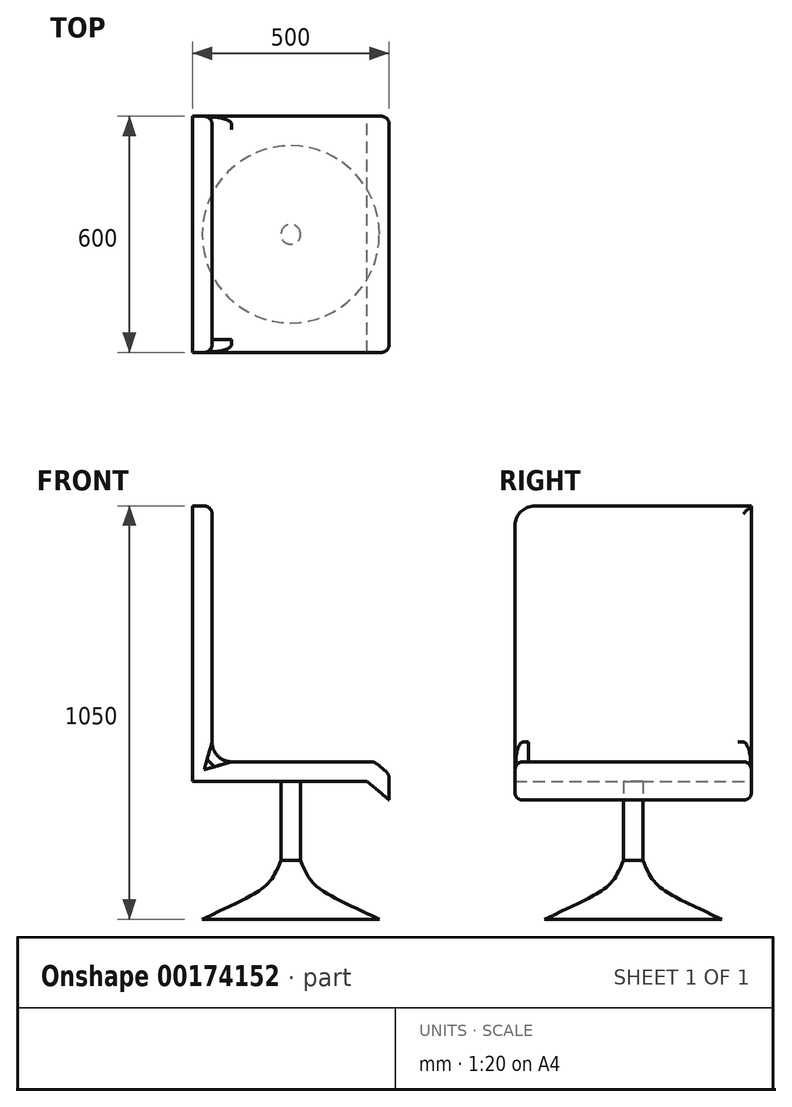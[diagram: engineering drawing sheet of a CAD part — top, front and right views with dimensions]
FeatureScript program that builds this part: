
annotation { "Feature Type Name" : "Feature", "Feature Type Description" : "" }
export const myFeature = defineFeature(function(context is Context, id is Id, definition is map)
    precondition{}
    {
        {
            var Q0;
            Q0=qCreatedBy(makeId("Top.planeOp"),FACE);
            var sketch = newSketch(context, id + "F0", { "sketchPlane" : qUnion([Q0])});
            skCircle(sketch, "E0", {"center": v(0, 0) * mm, "radius": 225 * mm});
            skSolve(sketch);
        }
        {
            var Q0;
            Q0=qCreatedBy(makeId("Top.planeOp"),FACE);
            cPlane(context, id + "F1", {"entities" : qUnion([Q0]), "cplaneType" : CPlaneType.OFFSET, "offset" : 150 * mm, "width" : 150 * mm, "height" : 150 * mm});
        }
        {
            var Q0;
            Q0=qCreatedBy(id+"F1.planeOp",FACE);
            var sketch = newSketch(context, id + "F2", { "sketchPlane" : qUnion([Q0])});
            skCircle(sketch, "E1", {"center": v(0, 0) * mm, "radius": 25 * mm});
            skSolve(sketch);
        }
        {
            var Q0;
            Q0=qCreatedBy(makeId("Top.planeOp"),FACE);
            cPlane(context, id + "F3", {"entities" : qUnion([Q0]), "cplaneType" : CPlaneType.OFFSET, "offset" : 50 * mm, "width" : 150 * mm, "height" : 150 * mm});
        }
        {
            var Q0;
            Q0=qCreatedBy(id+"F3.planeOp",FACE);
            var sketch = newSketch(context, id + "F4", { "sketchPlane" : qUnion([Q0])});
            skCircle(sketch, "E2", {"center": v(0, 0) * mm, "radius": 120 * mm});
            skSolve(sketch);
        }
        {
            var Q0;
            Q0=qCreatedBy(makeId("Top.planeOp"),FACE);
            cPlane(context, id + "F5", {"entities" : qUnion([Q0]), "cplaneType" : CPlaneType.OFFSET, "offset" : 100 * mm, "width" : 150 * mm, "height" : 150 * mm});
        }
        {
            var Q0;
            Q0=qCreatedBy(id+"F5.planeOp",FACE);
            var sketch = newSketch(context, id + "F6", { "sketchPlane" : qUnion([Q0])});
            skCircle(sketch, "E3", {"center": v(0, 0) * mm, "radius": 50 * mm});
            skSolve(sketch);
        }
        {
            var Q0;
            Q0=makeQuery(id+"F0.imprint","IMPRINT",FACE,{"disambiguationData":[TD([[makeQuery(id+"F0.imprint","IMPRINT",EDGE,{"derivedFrom":sQuery(id+"F0.wireOp",EDGE,"E0")}),1.0]])]});
            var Q1;
            Q1=makeQuery(id+"F4.imprint","IMPRINT",FACE,{"disambiguationData":[TD([[makeQuery(id+"F4.imprint","IMPRINT",EDGE,{"derivedFrom":sQuery(id+"F4.wireOp",EDGE,"E2")}),1.0]])]});
            var Q2;
            Q2=makeQuery(id+"F6.imprint","IMPRINT",FACE,{"disambiguationData":[TD([[makeQuery(id+"F6.imprint","IMPRINT",EDGE,{"derivedFrom":sQuery(id+"F6.wireOp",EDGE,"E3")}),1.0]])]});
            var Q3;
            Q3=makeQuery(id+"F2.imprint","IMPRINT",FACE,{"disambiguationData":[TD([[makeQuery(id+"F2.imprint","IMPRINT",EDGE,{"derivedFrom":sQuery(id+"F2.wireOp",EDGE,"E1")}),1.0]])]});
            loft(context, id + "F7", {"sheetProfilesArray" : [{ "sheetProfileEntities" : qUnion([Q0]) }, { "sheetProfileEntities" : qUnion([Q1]) }, { "sheetProfileEntities" : qUnion([Q2]) }, { "sheetProfileEntities" : qUnion([Q3]) }]});
        }
        {
            var Q0;
            Q0=makeQuery(id+"F7.opLoft","CAP_FACE",FACE,{"disambiguationData":[OSD([makeQuery(id+"F2.imprint","IMPRINT",FACE,{"disambiguationData":[TD([[makeQuery(id+"F2.imprint","IMPRINT",EDGE,{"derivedFrom":sQuery(id+"F2.wireOp",EDGE,"E1")}),1.0]])]})])],"isStart":true});
            extrude(context, id + "F8", {"entities" : qUnion([Q0]), "operationType" : NewBodyOperationType.ADD, "depth" : 200 * mm});
        }
        {
            var Q0;
            Q0=qCreatedBy(makeId("Front.planeOp"),FACE);
            var sketch = newSketch(context, id + "F9", { "sketchPlane" : qUnion([Q0])});
            skLineSegment(sketch, "E4", {"start": v(193.5, 350) * mm, "end": v(-250, 350) * mm});
            skLineSegment(sketch, "E5", {"start": v(-250, 350) * mm, "end": v(-250, 1050) * mm});
            skLineSegment(sketch, "E6", {"start": v(-250, 1050) * mm, "end": v(-200, 1050) * mm});
            skLineSegment(sketch, "E7", {"start": v(-200, 1050) * mm, "end": v(-200, 400) * mm});
            skLineSegment(sketch, "E8", {"start": v(-200, 400) * mm, "end": v(211.7, 400) * mm});
            skLineSegment(sketch, "E9", {"start": v(211.7, 400) * mm, "end": v(250, 367.86) * mm});
            skLineSegment(sketch, "E10", {"start": v(250, 367.86) * mm, "end": v(250, 302.6) * mm});
            skLineSegment(sketch, "E11", {"start": v(250, 302.6) * mm, "end": v(193.5, 350) * mm});
            skSolve(sketch);
        }
        {
            var Q0;
            Q0=makeQuery(id+"F9.imprint","IMPRINT",FACE,{"disambiguationData":[TD([[makeQuery(id+"F9.imprint","IMPRINT",EDGE,{"derivedFrom":sQuery(id+"F9.wireOp",EDGE,"E4")}),-1.0]])]});
            extrude(context, id + "F10", {"entities" : qUnion([Q0]), "operationType" : NewBodyOperationType.ADD, "endBound" : BoundingType.SYMMETRIC, "depth" : 600 * mm});
        }
        {
            var Q0;
            Q0=makeQuery(id+"F10.opExtrude","SWEPT_EDGE",EDGE,{"disambiguationData":[OSD([sQuery(id+"F9.wireOp",EDGE,"E8"),sQuery(id+"F9.wireOp",EDGE,"E9")])]});
            var Q1;
            Q1=makeQuery(id+"F10.opExtrude","SWEPT_EDGE",EDGE,{"disambiguationData":[OSD([sQuery(id+"F9.wireOp",EDGE,"E9"),sQuery(id+"F9.wireOp",EDGE,"E10")])]});
            var Q2;
            Q2=makeQuery(id+"F10.opExtrude","CAP_EDGE",EDGE,{"disambiguationData":[OSD([sQuery(id+"F9.wireOp",EDGE,"E10")])],"isStart":false});
            var Q3;
            Q3=makeQuery(id+"F10.opExtrude","CAP_EDGE",EDGE,{"disambiguationData":[OSD([sQuery(id+"F9.wireOp",EDGE,"E10")])],"isStart":true});
            var Q4;
            Q4=makeQuery(id+"F10.opExtrude","CAP_EDGE",EDGE,{"disambiguationData":[OSD([sQuery(id+"F9.wireOp",EDGE,"E9")])],"isStart":false});
            var Q5;
            Q5=makeQuery(id+"F10.opExtrude","CAP_EDGE",EDGE,{"disambiguationData":[OSD([sQuery(id+"F9.wireOp",EDGE,"E9")])],"isStart":true});
            var Q6;
            Q6=makeQuery(id+"F10.opExtrude","CAP_EDGE",EDGE,{"disambiguationData":[OSD([sQuery(id+"F9.wireOp",EDGE,"E8")])],"isStart":false});
            var Q7;
            Q7=makeQuery(id+"F10.opExtrude","CAP_EDGE",EDGE,{"disambiguationData":[OSD([sQuery(id+"F9.wireOp",EDGE,"E7")])],"isStart":false});
            var Q8;
            Q8=makeQuery(id+"F10.opExtrude","SWEPT_EDGE",EDGE,{"disambiguationData":[OSD([sQuery(id+"F9.wireOp",EDGE,"E6"),sQuery(id+"F9.wireOp",EDGE,"E7")])]});
            var Q9;
            Q9=makeQuery(id+"F10.opExtrude","CAP_EDGE",EDGE,{"disambiguationData":[OSD([sQuery(id+"F9.wireOp",EDGE,"E7")])],"isStart":true});
            var Q10;
            Q10=makeQuery(id+"F10.opExtrude","CAP_EDGE",EDGE,{"disambiguationData":[OSD([sQuery(id+"F9.wireOp",EDGE,"E8")])],"isStart":true});
            fillet(context, id + "F11", {"entities" : qUnion([Q0, Q1, Q2, Q3, Q4, Q5, Q6, Q7, Q8, Q9, Q10]), "radius" : 20 * mm, "tangentPropagation" : true, "allowEdgeOverflow" : false});
        }
        {
            var Q0;
            Q0=makeQuery(id+"F10.opExtrude","CAP_EDGE",EDGE,{"disambiguationData":[OSD([sQuery(id+"F9.wireOp",EDGE,"E6")])],"isStart":false});
            var Q1;
            {var subQ0=sQuery(id+"F9.wireOp",EDGE,"E6");Q1=makeQuery(id+"F11.opFillet","BLEND_EDGE",EDGE,{"blendedFrom":[makeQuery(id+"F10.opExtrude","SWEPT_EDGE",EDGE,{"disambiguationData":[OSD([subQ0,sQuery(id+"F9.wireOp",EDGE,"E7")])]}),makeQuery(id+"F10.opExtrude","SWEPT_FACE",FACE,{"disambiguationData":[OSD([subQ0])]})],"blendedInto":[makeQuery(id+"F10.opExtrude","SWEPT_FACE",FACE,{"disambiguationData":[OSD([subQ0])]})]});}
            var Q2;
            Q2=makeQuery(id+"F10.opExtrude","SWEPT_EDGE",EDGE,{"disambiguationData":[OSD([sQuery(id+"F9.wireOp",EDGE,"E7"),sQuery(id+"F9.wireOp",EDGE,"E8")])]});
            fillet(context, id + "F12", {"entities" : qUnion([Q0, Q1, Q2]), "radius" : 50 * mm, "tangentPropagation" : true, "allowEdgeOverflow" : false});
        }
    });
